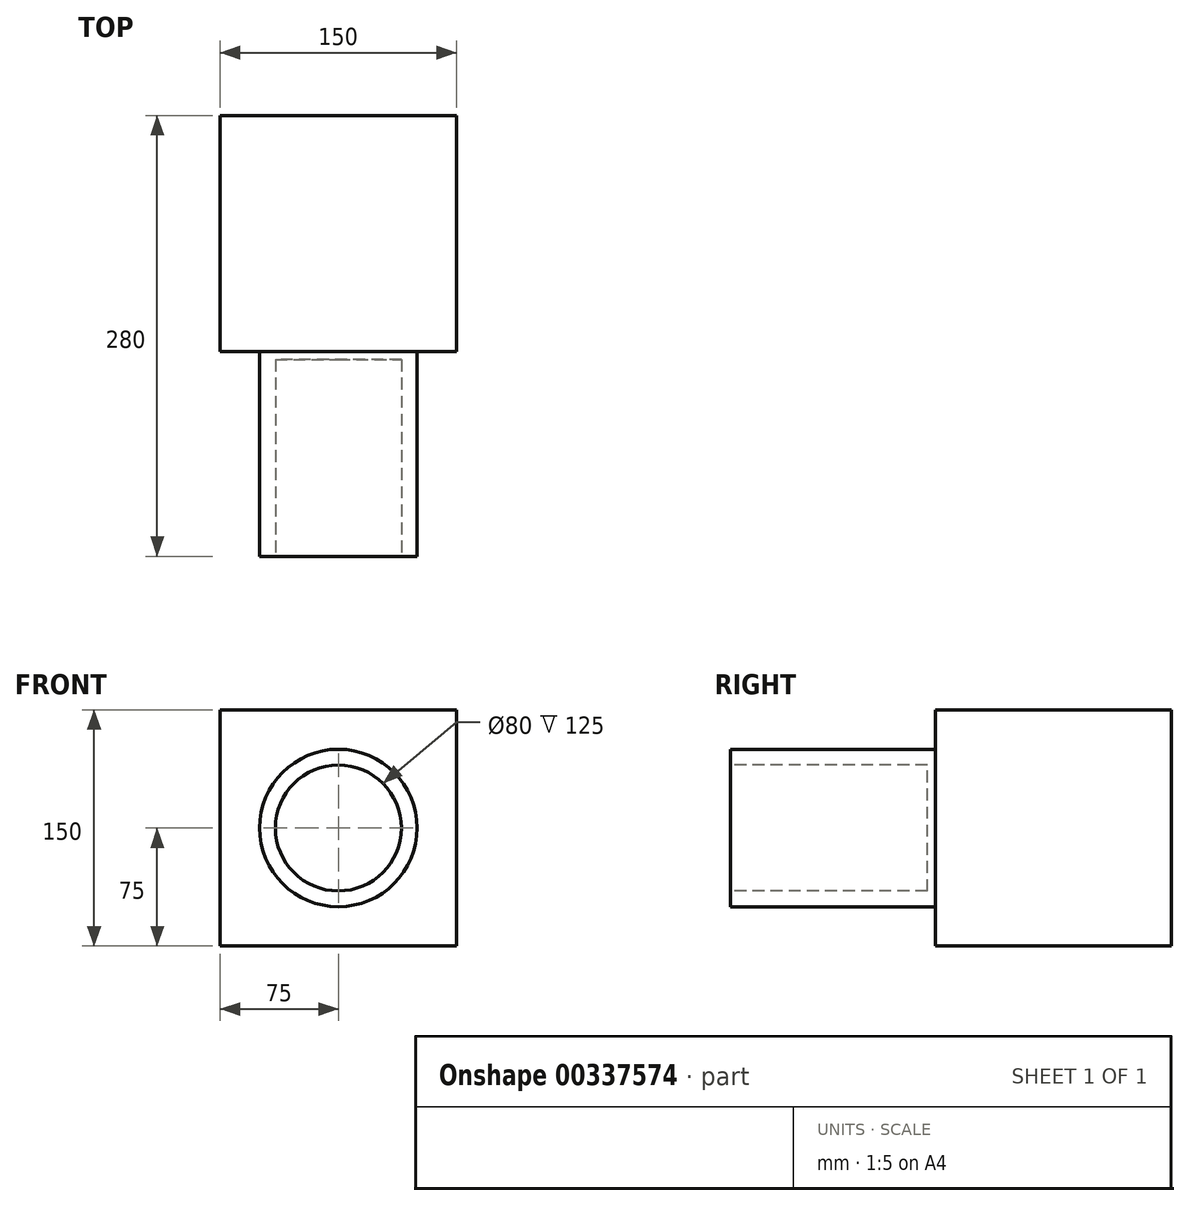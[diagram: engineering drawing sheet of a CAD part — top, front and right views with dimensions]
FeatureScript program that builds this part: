
annotation { "Feature Type Name" : "Feature", "Feature Type Description" : "" }
export const myFeature = defineFeature(function(context is Context, id is Id, definition is map)
    precondition{}
    {
        {
            var Q0;
            Q0=qCreatedBy(makeId("Top.planeOp"),FACE);
            var sketch = newSketch(context, id + "F0", { "sketchPlane" : qUnion([Q0])});
            skLineSegment(sketch, "E0.bottom", {"start": v(75, 75) * mm, "end": v(-75, 75) * mm});
            skLineSegment(sketch, "E0.top", {"start": v(75, -75) * mm, "end": v(-75, -75) * mm});
            skLineSegment(sketch, "E0.left", {"start": v(75, 75) * mm, "end": v(75, -75) * mm});
            skLineSegment(sketch, "E0.right", {"start": v(-75, 75) * mm, "end": v(-75, -75) * mm});
            skPoint(sketch, "E0.middle", {"position": v(0, 0) * mm});
            skSolve(sketch);
        }
        {
            var Q0;
            Q0=makeQuery(id+"F0.imprint","IMPRINT",FACE,{"disambiguationData":[TD([[makeQuery(id+"F0.imprint","IMPRINT",EDGE,{"derivedFrom":sQuery(id+"F0.wireOp",EDGE,"E0.bottom")}),1.0]])]});
            extrude(context, id + "F1", {"entities" : qUnion([Q0]), "depth" : 150 * mm});
        }
        {
            var Q0;
            Q0=makeQuery(id+"F1.opExtrude","SWEPT_FACE",FACE,{"disambiguationData":[OSD([sQuery(id+"F0.wireOp",EDGE,"E0.top")])]});
            var sketch = newSketch(context, id + "F2", { "sketchPlane" : qUnion([Q0])});
            skSolve(sketch);
        }
        {
            var Q0;
            {var subQ0=sQuery(id+"F0.wireOp",EDGE,"E0.top");Q0=makeQuery(id+"F2.imprint","IMPRINT",FACE,{"disambiguationData":[TD([[makeQuery(id+"F2.imprint","IMPRINT",EDGE,{"derivedFrom":makeQuery(id+"F1.opExtrude","CAP_EDGE",EDGE,{"disambiguationData":[OSD([subQ0])],"isStart":true})}),-1.0]])]});}
            var sketch = newSketch(context, id + "F3", { "sketchPlane" : qUnion([Q0])});
            skCircle(sketch, "E1", {"center": v(0, 75) * mm, "radius": 50 * mm});
            skLineSegment(sketch, "E2.0", {"start": v(-75, 150) * mm, "end": v(-75, 0) * mm});
            skLineSegment(sketch, "E3", {"start": v(-75, 0) * mm, "end": v(75, 150) * mm, "construction": true});
            skSolve(sketch);
        }
        {
            var Q0;
            Q0=qSketchRegion(id+"F3",true);
            extrude(context, id + "F4", {"entities" : qUnion([Q0]), "operationType" : NewBodyOperationType.ADD, "depth" : 130 * mm});
        }
        {
            var Q0;
            Q0=makeQuery(id+"F4.opExtrude","CAP_FACE",FACE,{"disambiguationData":[OSD([sQuery(id+"F3.wireOp",EDGE,"E1")])],"isStart":false});
            var sketch = newSketch(context, id + "F5", { "sketchPlane" : qUnion([Q0])});
            skCircle(sketch, "E4.0", {"center": v(0, 75) * mm, "radius": 50 * mm});
            skCircle(sketch, "E5", {"center": v(0, 75) * mm, "radius": 40 * mm});
            skSolve(sketch);
        }
        {
            var Q0;
            Q0=makeQuery(id+"F5.imprint","IMPRINT",FACE,{"disambiguationData":[TD([[makeQuery(id+"F5.imprint","IMPRINT",EDGE,{"derivedFrom":sQuery(id+"F5.wireOp",EDGE,"E5")}),1.0]])]});
            extrude(context, id + "F6", {"entities" : qUnion([Q0]), "operationType" : NewBodyOperationType.REMOVE, "oppositeDirection" : true, "depth" : 125 * mm});
        }
    });
